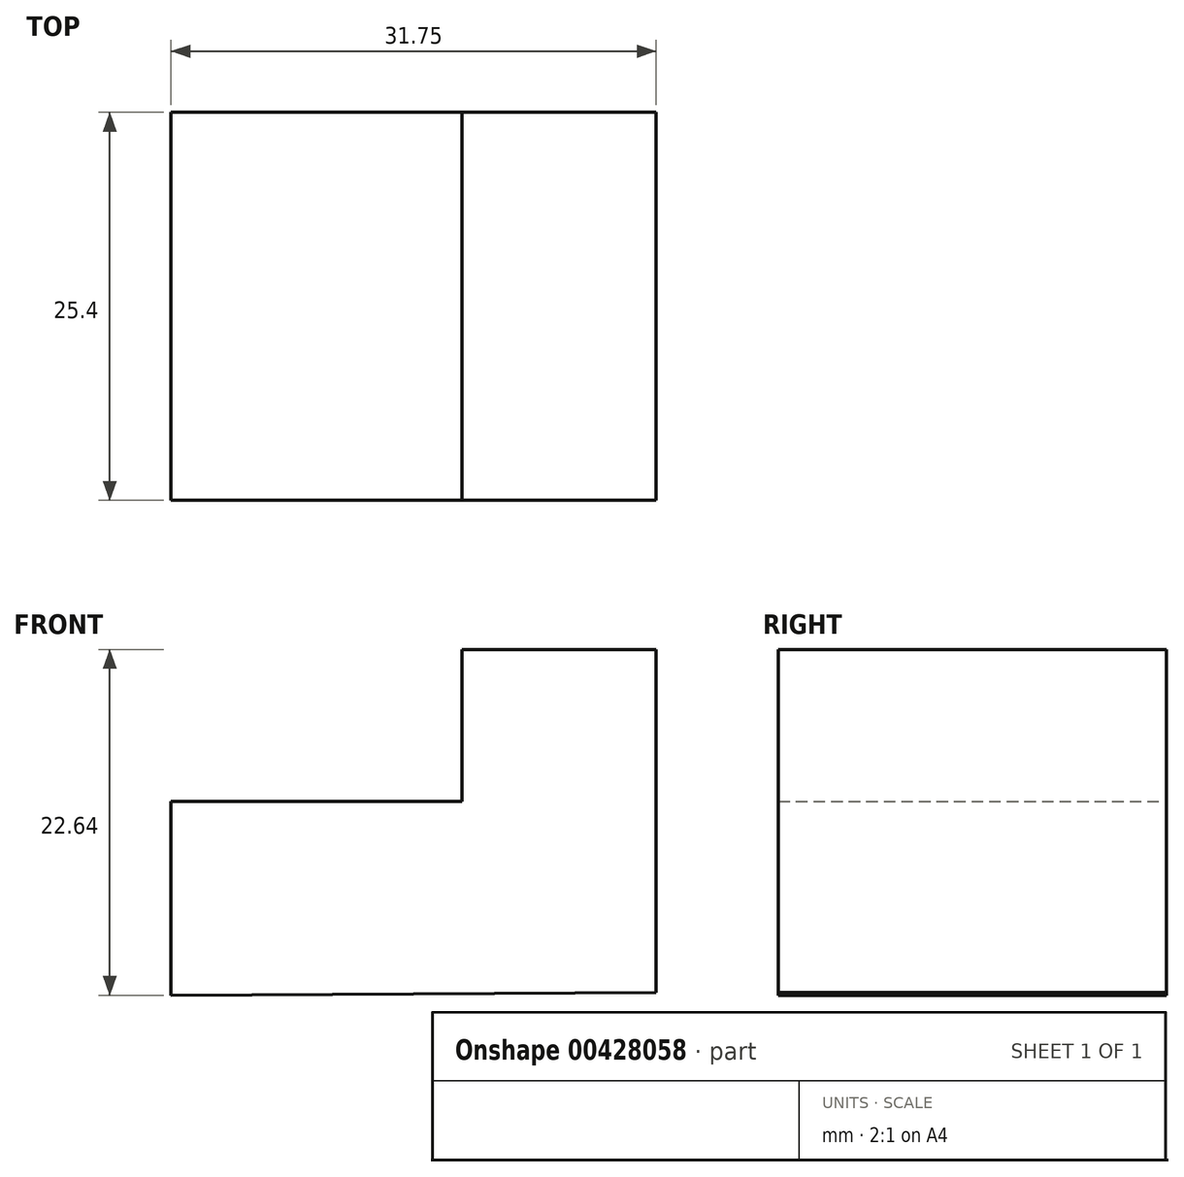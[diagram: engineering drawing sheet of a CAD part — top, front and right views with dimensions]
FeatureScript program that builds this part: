
annotation { "Feature Type Name" : "Feature", "Feature Type Description" : "" }
export const myFeature = defineFeature(function(context is Context, id is Id, definition is map)
    precondition{}
    {
        {
            var Q0;
            Q0=qCreatedBy(makeId("Front.planeOp"),FACE);
            var sketch = newSketch(context, id + "F0", { "sketchPlane" : qUnion([Q0])});
            skLineSegment(sketch, "E0", {"start": v(-48.54, -42.87) * mm, "end": v(-48.54, -30.17) * mm});
            skLineSegment(sketch, "E1", {"start": v(-48.54, -30.17) * mm, "end": v(-29.49, -30.17) * mm});
            skLineSegment(sketch, "E2", {"start": v(-29.49, -30.17) * mm, "end": v(-29.49, -20.23) * mm});
            skLineSegment(sketch, "E3", {"start": v(-29.49, -20.23) * mm, "end": v(-16.79, -20.23) * mm});
            skLineSegment(sketch, "E4", {"start": v(-16.79, -20.23) * mm, "end": v(-16.79, -42.68) * mm});
            skLineSegment(sketch, "E5", {"start": v(-16.79, -42.68) * mm, "end": v(-48.54, -42.87) * mm});
            skSolve(sketch);
        }
        {
            var Q0;
            Q0 = qSketchRegion(id + "FDECT01pGmXB7pc_0", true);
            var Q1;
            Q1=makeQuery(id+"F0.imprint","IMPRINT",FACE,{"disambiguationData":[TD([[makeQuery(id+"F0.imprint","IMPRINT",EDGE,{"derivedFrom":sQuery(id+"F0.wireOp",EDGE,"E0")}),-1.0]])]});
            extrude(context, id + "F1", {"entities" : qUnion([Q0, Q1]), "depth" : 25.4 * mm});
        }
    });
